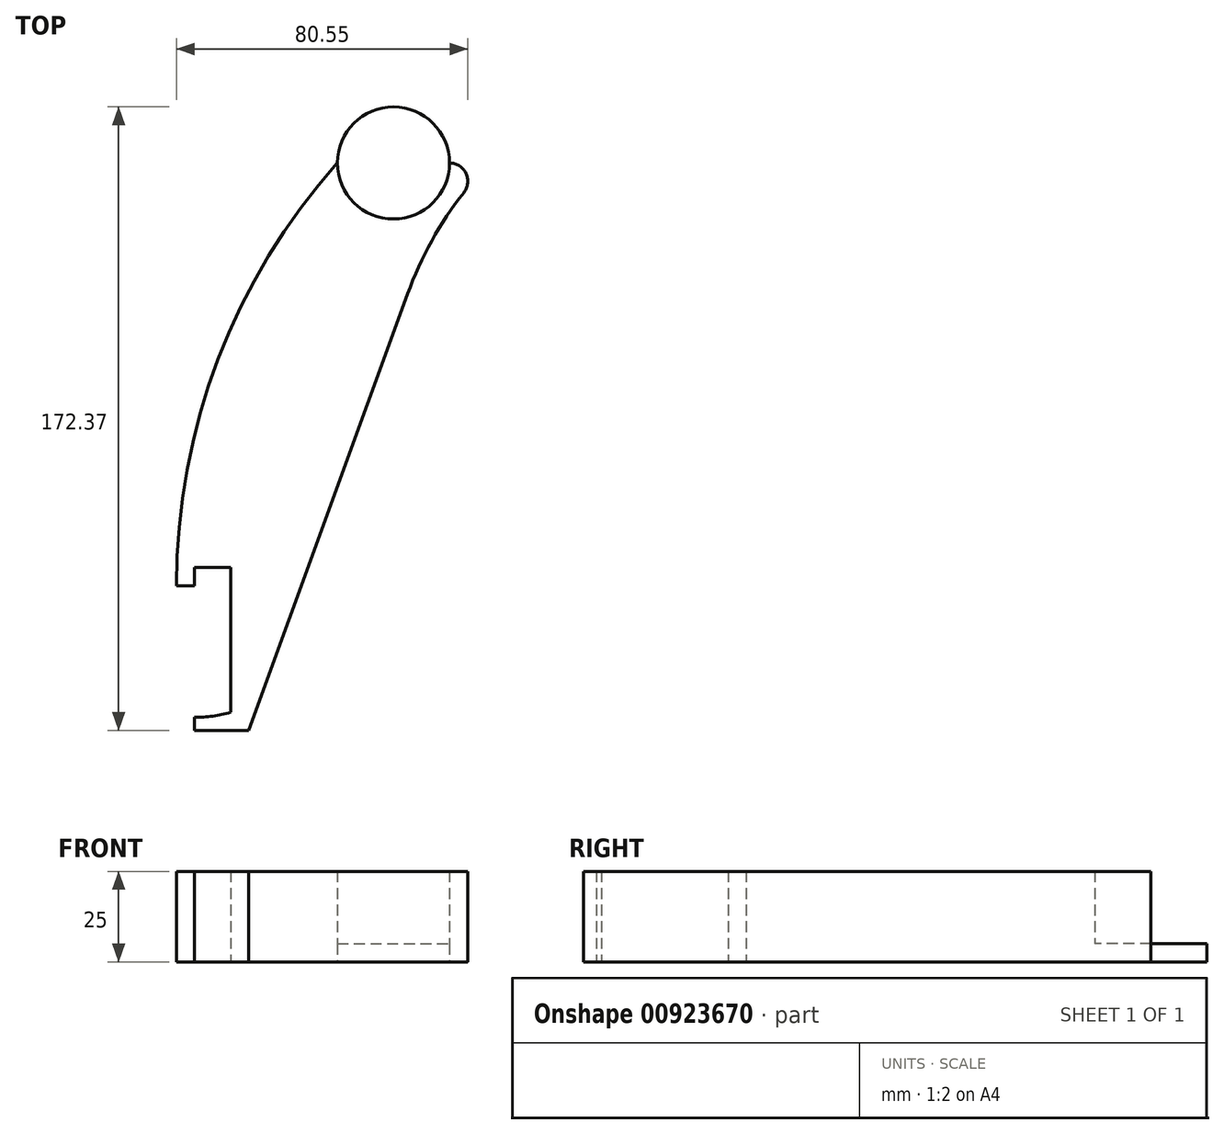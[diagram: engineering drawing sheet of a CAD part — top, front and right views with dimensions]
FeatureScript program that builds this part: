
annotation { "Feature Type Name" : "Feature", "Feature Type Description" : "" }
export const myFeature = defineFeature(function(context is Context, id is Id, definition is map)
    precondition{}
    {
        {
            var Q0;
            Q0=qCreatedBy(makeId("Top.planeOp"),FACE);
            var sketch = newSketch(context, id + "F0", { "sketchPlane" : qUnion([Q0])});
            skLineSegment(sketch, "E0.bottom", {"start": v(0, 0) * mm, "end": v(-10, 0) * mm});
            skLineSegment(sketch, "E0.top", {"start": v(0, -40) * mm, "end": v(-10, -40) * mm, "construction": true});
            skLineSegment(sketch, "E0.left", {"start": v(0, 0) * mm, "end": v(0, -40) * mm});
            skLineSegment(sketch, "E0.right", {"start": v(-10, 0) * mm, "end": v(-10, -5) * mm});
            skLineSegment(sketch, "E1", {"start": v(-10, -5) * mm, "end": v(-10, -40) * mm, "construction": true});
            skLineSegment(sketch, "E2", {"start": v(-10, -5) * mm, "end": v(-15, -5) * mm});
            skLineSegment(sketch, "E3", {"start": v(-15, -5) * mm, "end": v(-15, -5) * mm});
            skArc(sketch, "E4", {"start": v(0, -40) * mm, "mid": v(-4.95, -41.05) * mm, "end": v(-10, -41.4) * mm});
            skLineSegment(sketch, "E5", {"start": v(-10, -41.4) * mm, "end": v(-10, -45) * mm});
            skLineSegment(sketch, "E6", {"start": v(-10, -45) * mm, "end": v(5, -45) * mm});
            skLineSegment(sketch, "E7", {"start": v(5, -45) * mm, "end": v(48.93, 75.68) * mm});
            skArc(sketch, "E8", {"start": v(48.93, 75.68) * mm, "mid": v(55.6, 90.3) * mm, "end": v(64.48, 103.7) * mm});
            skArc(sketch, "E9", {"start": v(-15, -5) * mm, "mid": v(-3.5, 57.53) * mm, "end": v(29.5, 111.87) * mm});
            skCircle(sketch, "E10", {"center": v(45, 100.37) * mm, "radius": 100 * mm, "construction": true});
            skCircle(sketch, "E11", {"center": v(45, 100.37) * mm, "radius": 25 * mm, "construction": true});
            skCircle(sketch, "E12", {"center": v(45, 111.87) * mm, "radius": 13.5 * mm, "construction": true});
            skCircle(sketch, "E13.0", {"center": v(45, 111.87) * mm, "radius": 15.5 * mm});
            skLineSegment(sketch, "E14", {"start": v(45, 100.37) * mm, "end": v(45, 125.37) * mm, "construction": true});
            skLineSegment(sketch, "E15", {"start": v(45, 111.87) * mm, "end": v(45, 125.37) * mm, "construction": true});
            skLineSegment(sketch, "E16", {"start": v(29.5, 111.87) * mm, "end": v(60.5, 111.87) * mm});
            skLineSegment(sketch, "E17", {"start": v(60.5, 111.87) * mm, "end": v(60.5, 111.87) * mm});
            skArc(sketch, "E18", {"start": v(64.48, 103.7) * mm, "mid": v(65.04, 109.03) * mm, "end": v(60.5, 111.87) * mm});
            skSolve(sketch);
        }
        {
            var Q0;
            Q0=makeQuery(id+"F0.imprint","IMPRINT",FACE,{"disambiguationData":[TD([[makeQuery(id+"F0.imprint","IMPRINT",EDGE,{"derivedFrom":sQuery(id+"F0.wireOp",EDGE,"E0.bottom")}),-1.0]])]});
            extrude(context, id + "F1", {"entities" : qUnion([Q0]), "depth" : 25 * mm, "offsetDistance" : 25 * mm});
        }
        {
            var Q0;
            {var subQ0=sQuery(id+"F0.wireOp",EDGE,"E16");Q0=makeQuery(id+"F0.imprint","IMPRINT",FACE,{"disambiguationData":[TD([[makeQuery(id+"F0.imprint","IMPRINT",EDGE,{"derivedFrom":subQ0}),-1.0]])]});}
            var Q1;
            {var subQ0=sQuery(id+"F0.wireOp",EDGE,"E16");Q1=makeQuery(id+"F0.imprint","IMPRINT",FACE,{"disambiguationData":[TD([[makeQuery(id+"F0.imprint","IMPRINT",EDGE,{"derivedFrom":subQ0}),1.0]])]});}
            extrude(context, id + "F2", {"entities" : qUnion([Q0, Q1]), "operationType" : NewBodyOperationType.ADD, "depth" : 5 * mm, "offsetDistance" : 25 * mm});
        }
    });
